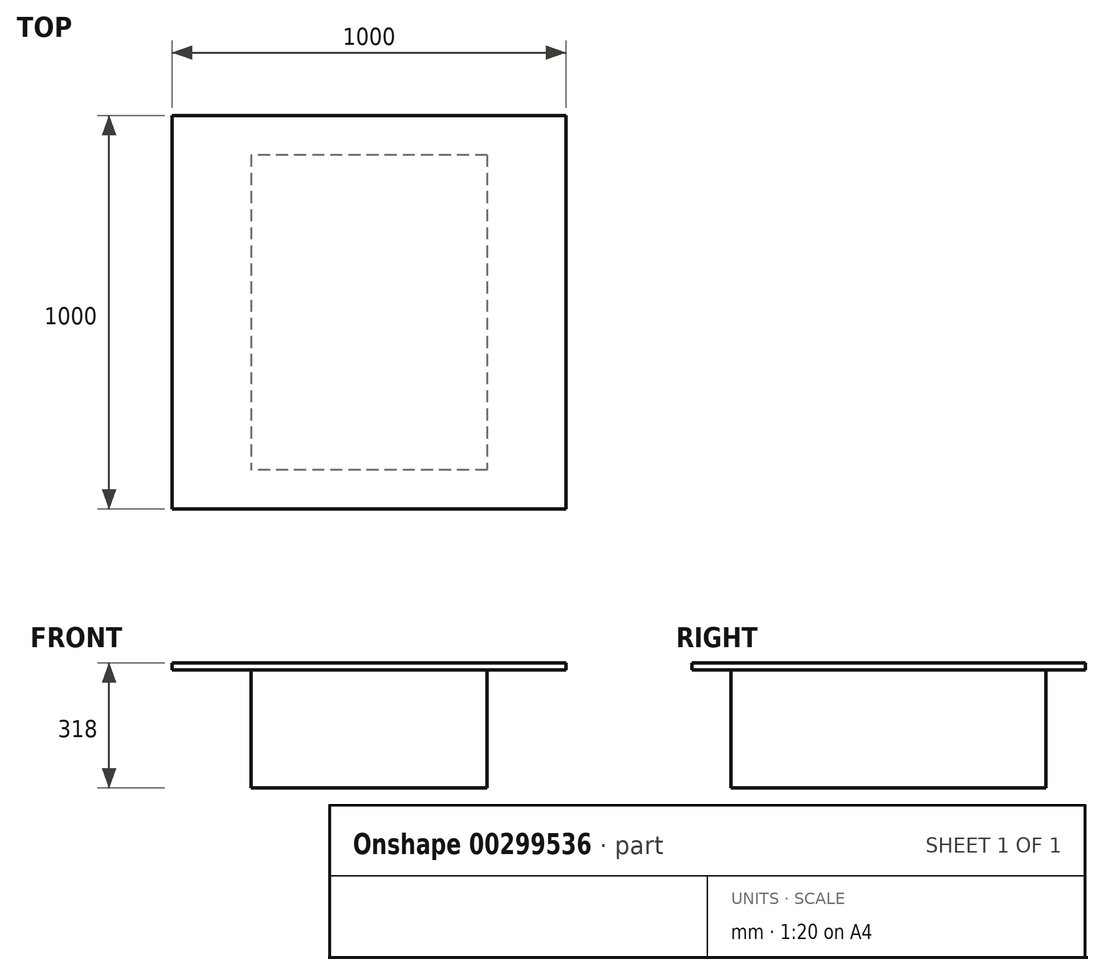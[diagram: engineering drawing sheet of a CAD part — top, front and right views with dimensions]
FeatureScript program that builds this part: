
annotation { "Feature Type Name" : "Feature", "Feature Type Description" : "" }
export const myFeature = defineFeature(function(context is Context, id is Id, definition is map)
    precondition{}
    {
        {
            assignVariable(context, id + "F0", {"name" : "TableThickness", "anyValue" : 18});
        }
        {
            assignVariable(context, id + "F1", {"name" : "BoxHeight", "anyValue" : 300});
        }
        {
            var Q0;
            Q0=qCreatedBy(makeId("Top.planeOp"),FACE);
            var sketch = newSketch(context, id + "F2", { "sketchPlane" : qUnion([Q0])});
            skLineSegment(sketch, "E0.bottom", {"start": v(500, 500) * mm, "end": v(-500, 500) * mm});
            skLineSegment(sketch, "E0.top", {"start": v(500, -500) * mm, "end": v(-500, -500) * mm});
            skLineSegment(sketch, "E0.left", {"start": v(500, 500) * mm, "end": v(500, -500) * mm});
            skLineSegment(sketch, "E0.right", {"start": v(-500, 500) * mm, "end": v(-500, -500) * mm});
            skPoint(sketch, "E0.middle", {"position": v(0, 0) * mm});
            skLineSegment(sketch, "E1.bottom", {"start": v(300, 400) * mm, "end": v(-300, 400) * mm});
            skLineSegment(sketch, "E1.top", {"start": v(300, -400) * mm, "end": v(-300, -400) * mm});
            skLineSegment(sketch, "E1.left", {"start": v(300, 400) * mm, "end": v(300, -400) * mm});
            skLineSegment(sketch, "E1.right", {"start": v(-300, 400) * mm, "end": v(-300, -400) * mm});
            skSolve(sketch);
        }
        {
            var Q0;
            Q0=makeQuery(id+"F2.imprint","IMPRINT",FACE,{"disambiguationData":[TD([[makeQuery(id+"F2.imprint","IMPRINT",EDGE,{"derivedFrom":sQuery(id+"F2.wireOp",EDGE,"E1.bottom")}),1.0]])]});
            var Q1;
            Q1=makeQuery(id+"F2.imprint","IMPRINT",FACE,{"disambiguationData":[TD([[makeQuery(id+"F2.imprint","IMPRINT",EDGE,{"derivedFrom":sQuery(id+"F2.wireOp",EDGE,"E0.bottom")}),1.0]])]});
            extrude(context, id + "F3", {"entities" : qUnion([Q0, Q1]), "depth" : (getVariable(context, 'TableThickness')) * mm});
        }
        {
            var Q0;
            Q0=makeQuery(id+"F2.imprint","IMPRINT",FACE,{"disambiguationData":[TD([[makeQuery(id+"F2.imprint","IMPRINT",EDGE,{"derivedFrom":sQuery(id+"F2.wireOp",EDGE,"E1.bottom")}),1.0]])]});
            extrude(context, id + "F4", {"entities" : qUnion([Q0]), "operationType" : NewBodyOperationType.ADD, "oppositeDirection" : true, "depth" : (getVariable(context, 'BoxHeight')) * mm});
        }
    });
